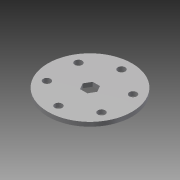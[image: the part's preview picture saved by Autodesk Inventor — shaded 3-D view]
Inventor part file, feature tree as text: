
AUTODESK INVENTOR PART (.ipt)
format: ipt  version: 2013 (Build 170138000, 138)  size: 96,256 bytes
history: native  units: in
note: dims shown in document units (in); Inventor stores cm internally (conversion verified against a paired STEP export)
features: extrude x1, sketch x1
ambient origin geometry x8: Origin, YZ Plane, XZ Plane, XY Plane, X Axis, Y Axis, Z Axis, Center Point
feature tree (2):
  extrude  "Extrusion3"  Depth=0.22in
  sketch  "Sketch1"  dims[d0=0.375in d5=0.22in d7=2.3622in d9=360.0deg d22=0.375in d23=0.125in d24=0.0in d25=0.9375in]
